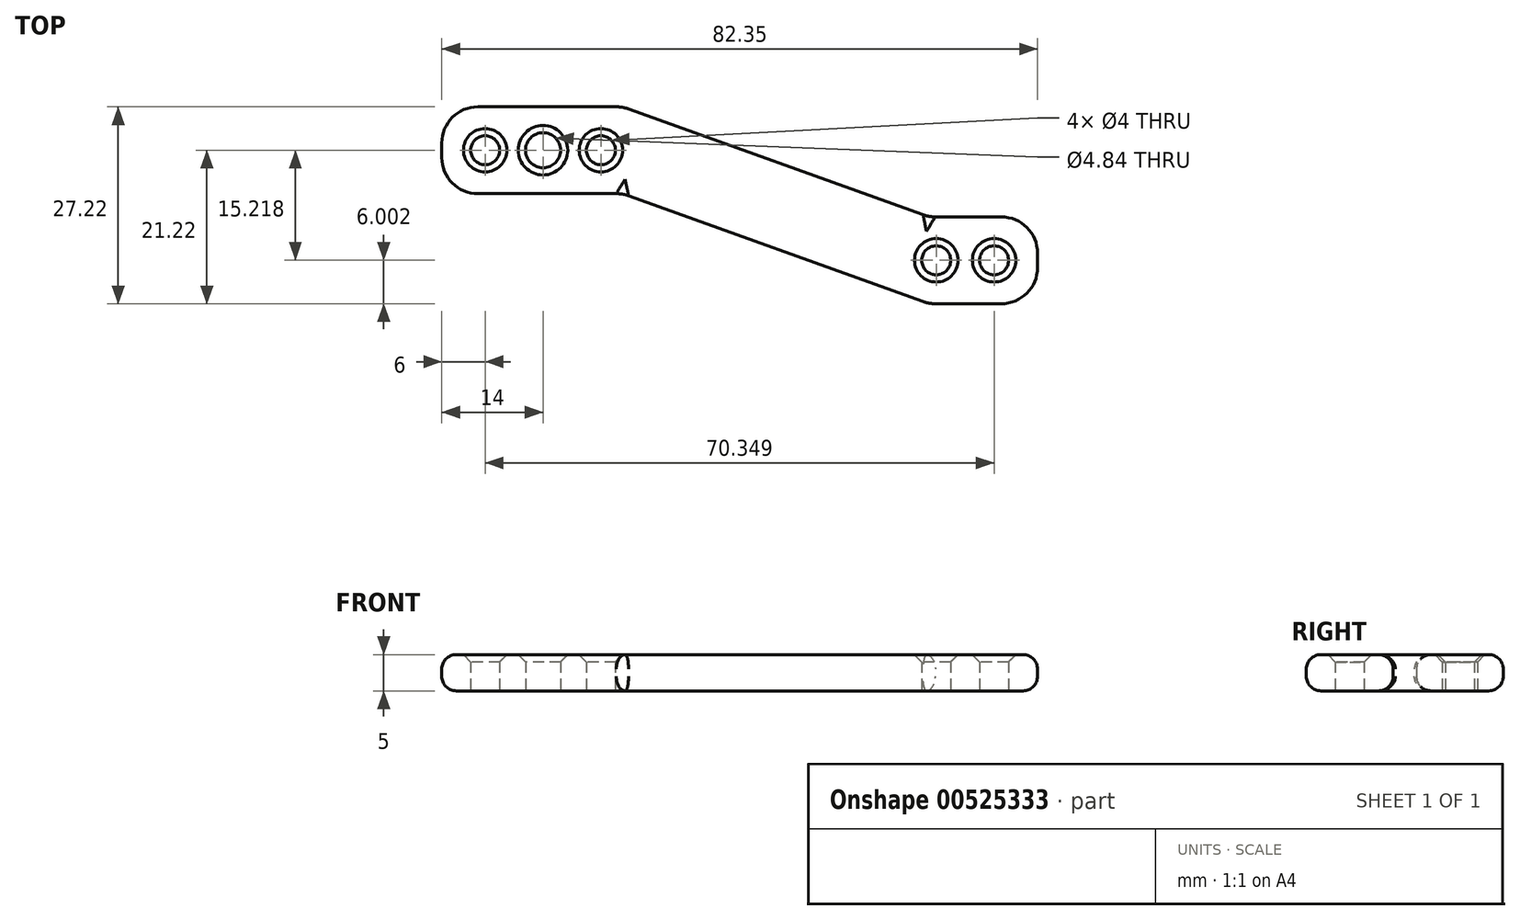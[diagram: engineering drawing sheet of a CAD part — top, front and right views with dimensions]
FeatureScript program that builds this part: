
annotation { "Feature Type Name" : "Feature", "Feature Type Description" : "" }
export const myFeature = defineFeature(function(context is Context, id is Id, definition is map)
    precondition{}
    {
        {
            var Q0;
            Q0=qCreatedBy(makeId("Top.planeOp"),FACE);
            var sketch = newSketch(context, id + "F0", { "sketchPlane" : qUnion([Q0])});
            skLineSegment(sketch, "E0.bottom", {"start": v(0, 0) * mm, "end": v(25, 0) * mm});
            skLineSegment(sketch, "E0.top", {"start": v(0, -12) * mm, "end": v(25, -12) * mm});
            skLineSegment(sketch, "E0.left", {"start": v(0, 0) * mm, "end": v(0, -12) * mm});
            skLineSegment(sketch, "E0.right", {"start": v(25, 0) * mm, "end": v(25, -12) * mm});
            skLineSegment(sketch, "E1", {"start": v(25, -12) * mm, "end": v(67.35, -27.22) * mm});
            skLineSegment(sketch, "E2", {"start": v(25, 0) * mm, "end": v(67.35, -15.22) * mm});
            skLineSegment(sketch, "E3", {"start": v(67.35, -15.22) * mm, "end": v(67.35, -27.22) * mm});
            skLineSegment(sketch, "E4.bottom", {"start": v(67.35, -27.22) * mm, "end": v(82.35, -27.22) * mm});
            skLineSegment(sketch, "E4.top", {"start": v(67.35, -15.22) * mm, "end": v(82.35, -15.22) * mm});
            skLineSegment(sketch, "E4.left", {"start": v(67.35, -27.22) * mm, "end": v(67.35, -15.22) * mm});
            skLineSegment(sketch, "E4.right", {"start": v(82.35, -27.22) * mm, "end": v(82.35, -15.22) * mm});
            skSolve(sketch);
        }
        {
            var Q0;
            Q0 = qSketchRegion(id + "F0", true);
            extrude(context, id + "F1", {"entities" : qUnion([Q0]), "depth" : 5 * mm, "offsetDistance" : 25 * mm});
        }
        {
            var Q0;
            Q0=qCreatedBy(makeId("Top.planeOp"),FACE);
            var sketch = newSketch(context, id + "F2", { "sketchPlane" : qUnion([Q0])});
            skCircle(sketch, "E5", {"center": v(6, -6) * mm, "radius": 2 * mm});
            skCircle(sketch, "E6", {"center": v(76.35, -21.22) * mm, "radius": 2 * mm});
            skCircle(sketch, "E7", {"center": v(14, -6) * mm, "radius": 2.42 * mm});
            skCircle(sketch, "E8", {"center": v(22, -6) * mm, "radius": 2 * mm});
            skCircle(sketch, "E9", {"center": v(68.35, -21.22) * mm, "radius": 2 * mm});
            skSolve(sketch);
        }
        {
            var Q0;
            Q0 = qSketchRegion(id + "F2", true);
            extrude(context, id + "F3", {"entities" : qUnion([Q0]), "operationType" : NewBodyOperationType.REMOVE, "depth" : 50 * mm, "offsetDistance" : 25 * mm});
        }
        {
            var Q0;
            Q0=makeQuery(id+"F1.opExtrude","CAP_EDGE",EDGE,{"disambiguationData":[OSD([sQuery(id+"F0.wireOp",EDGE,"E2")])],"isStart":false});
            var Q1;
            Q1=makeQuery(id+"F1.opExtrude","CAP_EDGE",EDGE,{"disambiguationData":[OSD([sQuery(id+"F0.wireOp",EDGE,"E0.bottom")])],"isStart":false});
            var Q2;
            Q2=makeQuery(id+"F1.opExtrude","CAP_EDGE",EDGE,{"disambiguationData":[OSD([sQuery(id+"F0.wireOp",EDGE,"E0.left")])],"isStart":false});
            var Q3;
            Q3=makeQuery(id+"F1.opExtrude","CAP_EDGE",EDGE,{"disambiguationData":[OSD([sQuery(id+"F0.wireOp",EDGE,"E0.top")])],"isStart":false});
            var Q4;
            Q4=makeQuery(id+"F1.opExtrude","CAP_EDGE",EDGE,{"disambiguationData":[OSD([sQuery(id+"F0.wireOp",EDGE,"E1")])],"isStart":false});
            var Q5;
            Q5=makeQuery(id+"F1.opExtrude","CAP_EDGE",EDGE,{"disambiguationData":[OSD([sQuery(id+"F0.wireOp",EDGE,"E4.bottom")])],"isStart":false});
            var Q6;
            Q6=makeQuery(id+"F1.opExtrude","CAP_EDGE",EDGE,{"disambiguationData":[OSD([sQuery(id+"F0.wireOp",EDGE,"E4.right")])],"isStart":false});
            var Q7;
            Q7=makeQuery(id+"F1.opExtrude","CAP_EDGE",EDGE,{"disambiguationData":[OSD([sQuery(id+"F0.wireOp",EDGE,"E4.top")])],"isStart":false});
            var Q8;
            Q8=makeQuery(id+"F1.opExtrude","CAP_EDGE",EDGE,{"disambiguationData":[OSD([sQuery(id+"F0.wireOp",EDGE,"E1")])],"isStart":true});
            var Q9;
            Q9=makeQuery(id+"F1.opExtrude","CAP_EDGE",EDGE,{"disambiguationData":[OSD([sQuery(id+"F0.wireOp",EDGE,"E0.top")])],"isStart":true});
            var Q10;
            Q10=makeQuery(id+"F1.opExtrude","CAP_EDGE",EDGE,{"disambiguationData":[OSD([sQuery(id+"F0.wireOp",EDGE,"E0.left")])],"isStart":true});
            var Q11;
            Q11=makeQuery(id+"F1.opExtrude","CAP_EDGE",EDGE,{"disambiguationData":[OSD([sQuery(id+"F0.wireOp",EDGE,"E0.bottom")])],"isStart":true});
            var Q12;
            Q12=makeQuery(id+"F1.opExtrude","CAP_EDGE",EDGE,{"disambiguationData":[OSD([sQuery(id+"F0.wireOp",EDGE,"E2")])],"isStart":true});
            var Q13;
            Q13=makeQuery(id+"F1.opExtrude","CAP_EDGE",EDGE,{"disambiguationData":[OSD([sQuery(id+"F0.wireOp",EDGE,"E4.top")])],"isStart":true});
            var Q14;
            Q14=makeQuery(id+"F1.opExtrude","CAP_EDGE",EDGE,{"disambiguationData":[OSD([sQuery(id+"F0.wireOp",EDGE,"E4.right")])],"isStart":true});
            var Q15;
            Q15=makeQuery(id+"F1.opExtrude","CAP_EDGE",EDGE,{"disambiguationData":[OSD([sQuery(id+"F0.wireOp",EDGE,"E4.bottom")])],"isStart":true});
            fillet(context, id + "F4", {"entities" : qUnion([Q0, Q1, Q2, Q3, Q4, Q5, Q6, Q7, Q8, Q9, Q10, Q11, Q12, Q13, Q14, Q15]), "radius" : 2 * mm, "tangentPropagation" : true, "allowEdgeOverflow" : false});
        }
        {
            var Q0;
            Q0=makeQuery(id+"F4.opFillet","BLEND_EDGE",EDGE,{"blendedFrom":[makeQuery(id+"F1.opExtrude","CAP_EDGE",EDGE,{"disambiguationData":[OSD([sQuery(id+"F0.wireOp",EDGE,"E0.top")])],"isStart":true}),makeQuery(id+"F1.opExtrude","CAP_EDGE",EDGE,{"disambiguationData":[OSD([sQuery(id+"F0.wireOp",EDGE,"E1")])],"isStart":true})],"blendedInto":[]});
            var Q1;
            Q1=makeQuery(id+"F1.opExtrude","SWEPT_EDGE",EDGE,{"disambiguationData":[OSD([sQuery(id+"F0.wireOp",EDGE,"E0.top"),sQuery(id+"F0.wireOp",EDGE,"E0.right"),sQuery(id+"F0.wireOp",EDGE,"E1")])]});
            var Q2;
            Q2=makeQuery(id+"F4.opFillet","BLEND_EDGE",EDGE,{"blendedFrom":[makeQuery(id+"F1.opExtrude","CAP_EDGE",EDGE,{"disambiguationData":[OSD([sQuery(id+"F0.wireOp",EDGE,"E0.top")])],"isStart":false}),makeQuery(id+"F1.opExtrude","CAP_EDGE",EDGE,{"disambiguationData":[OSD([sQuery(id+"F0.wireOp",EDGE,"E1")])],"isStart":false})],"blendedInto":[]});
            var Q3;
            Q3=makeQuery(id+"F4.opFillet","BLEND_EDGE",EDGE,{"blendedFrom":[makeQuery(id+"F1.opExtrude","CAP_EDGE",EDGE,{"disambiguationData":[OSD([sQuery(id+"F0.wireOp",EDGE,"E0.bottom")])],"isStart":true}),makeQuery(id+"F1.opExtrude","CAP_EDGE",EDGE,{"disambiguationData":[OSD([sQuery(id+"F0.wireOp",EDGE,"E2")])],"isStart":true})],"blendedInto":[]});
            var Q4;
            Q4=makeQuery(id+"F4.opFillet","BLEND_EDGE",EDGE,{"blendedFrom":[makeQuery(id+"F1.opExtrude","CAP_EDGE",EDGE,{"disambiguationData":[OSD([sQuery(id+"F0.wireOp",EDGE,"E1")])],"isStart":false}),makeQuery(id+"F1.opExtrude","CAP_EDGE",EDGE,{"disambiguationData":[OSD([sQuery(id+"F0.wireOp",EDGE,"E4.bottom")])],"isStart":false})],"blendedInto":[]});
            var Q5;
            Q5=makeQuery(id+"F4.opFillet","BLEND_EDGE",EDGE,{"blendedFrom":[makeQuery(id+"F1.opExtrude","CAP_EDGE",EDGE,{"disambiguationData":[OSD([sQuery(id+"F0.wireOp",EDGE,"E2")])],"isStart":true}),makeQuery(id+"F1.opExtrude","CAP_EDGE",EDGE,{"disambiguationData":[OSD([sQuery(id+"F0.wireOp",EDGE,"E4.top")])],"isStart":true})],"blendedInto":[]});
            var Q6;
            Q6=makeQuery(id+"F4.opFillet","BLEND_EDGE",EDGE,{"blendedFrom":[makeQuery(id+"F1.opExtrude","CAP_EDGE",EDGE,{"disambiguationData":[OSD([sQuery(id+"F0.wireOp",EDGE,"E2")])],"isStart":false}),makeQuery(id+"F1.opExtrude","CAP_EDGE",EDGE,{"disambiguationData":[OSD([sQuery(id+"F0.wireOp",EDGE,"E4.top")])],"isStart":false})],"blendedInto":[]});
            var Q7;
            Q7=makeQuery(id+"F4.opFillet","BLEND_EDGE",EDGE,{"blendedFrom":[makeQuery(id+"F1.opExtrude","CAP_EDGE",EDGE,{"disambiguationData":[OSD([sQuery(id+"F0.wireOp",EDGE,"E0.bottom")])],"isStart":false}),makeQuery(id+"F1.opExtrude","CAP_EDGE",EDGE,{"disambiguationData":[OSD([sQuery(id+"F0.wireOp",EDGE,"E2")])],"isStart":false})],"blendedInto":[]});
            var Q8;
            Q8=makeQuery(id+"F4.opFillet","BLEND_EDGE",EDGE,{"blendedFrom":[makeQuery(id+"F1.opExtrude","CAP_EDGE",EDGE,{"disambiguationData":[OSD([sQuery(id+"F0.wireOp",EDGE,"E1")])],"isStart":true}),makeQuery(id+"F1.opExtrude","CAP_EDGE",EDGE,{"disambiguationData":[OSD([sQuery(id+"F0.wireOp",EDGE,"E4.bottom")])],"isStart":true})],"blendedInto":[]});
            fillet(context, id + "F5", {"entities" : qUnion([Q0, Q1, Q2, Q3, Q4, Q5, Q6, Q7, Q8]), "radius" : 5 * mm, "tangentPropagation" : true, "allowEdgeOverflow" : false});
        }
        {
            var Q0;
            Q0=makeQuery(id+"F4.opFillet","BLEND_EDGE",EDGE,{"blendedFrom":[makeQuery(id+"F1.opExtrude","CAP_EDGE",EDGE,{"disambiguationData":[OSD([sQuery(id+"F0.wireOp",EDGE,"E4.bottom")])],"isStart":false}),makeQuery(id+"F1.opExtrude","CAP_EDGE",EDGE,{"disambiguationData":[OSD([sQuery(id+"F0.wireOp",EDGE,"E4.right")])],"isStart":false})],"blendedInto":[]});
            var Q1;
            Q1=makeQuery(id+"F4.opFillet","BLEND_EDGE",EDGE,{"blendedFrom":[makeQuery(id+"F1.opExtrude","CAP_EDGE",EDGE,{"disambiguationData":[OSD([sQuery(id+"F0.wireOp",EDGE,"E0.top")])],"isStart":false}),makeQuery(id+"F1.opExtrude","CAP_EDGE",EDGE,{"disambiguationData":[OSD([sQuery(id+"F0.wireOp",EDGE,"E0.left")])],"isStart":false})],"blendedInto":[]});
            var Q2;
            Q2=makeQuery(id+"F4.opFillet","BLEND_EDGE",EDGE,{"blendedFrom":[makeQuery(id+"F1.opExtrude","CAP_EDGE",EDGE,{"disambiguationData":[OSD([sQuery(id+"F0.wireOp",EDGE,"E0.bottom")])],"isStart":true}),makeQuery(id+"F1.opExtrude","CAP_EDGE",EDGE,{"disambiguationData":[OSD([sQuery(id+"F0.wireOp",EDGE,"E0.left")])],"isStart":true})],"blendedInto":[]});
            var Q3;
            Q3=makeQuery(id+"F4.opFillet","BLEND_EDGE",EDGE,{"blendedFrom":[makeQuery(id+"F1.opExtrude","CAP_EDGE",EDGE,{"disambiguationData":[OSD([sQuery(id+"F0.wireOp",EDGE,"E4.top")])],"isStart":false}),makeQuery(id+"F1.opExtrude","CAP_EDGE",EDGE,{"disambiguationData":[OSD([sQuery(id+"F0.wireOp",EDGE,"E4.right")])],"isStart":false})],"blendedInto":[]});
            var Q4;
            Q4=makeQuery(id+"F4.opFillet","BLEND_EDGE",EDGE,{"blendedFrom":[makeQuery(id+"F1.opExtrude","CAP_EDGE",EDGE,{"disambiguationData":[OSD([sQuery(id+"F0.wireOp",EDGE,"E4.bottom")])],"isStart":true}),makeQuery(id+"F1.opExtrude","CAP_EDGE",EDGE,{"disambiguationData":[OSD([sQuery(id+"F0.wireOp",EDGE,"E4.right")])],"isStart":true})],"blendedInto":[]});
            var Q5;
            Q5=makeQuery(id+"F4.opFillet","BLEND_EDGE",EDGE,{"blendedFrom":[makeQuery(id+"F1.opExtrude","CAP_EDGE",EDGE,{"disambiguationData":[OSD([sQuery(id+"F0.wireOp",EDGE,"E4.top")])],"isStart":true}),makeQuery(id+"F1.opExtrude","CAP_EDGE",EDGE,{"disambiguationData":[OSD([sQuery(id+"F0.wireOp",EDGE,"E4.right")])],"isStart":true})],"blendedInto":[]});
            fillet(context, id + "F6", {"entities" : qUnion([Q0, Q1, Q2, Q3, Q4, Q5]), "radius" : 5 * mm, "tangentPropagation" : true, "allowEdgeOverflow" : false});
        }
        {
            var Q0;
            Q0=makeQuery(id+"F3.boolean.opBoolean","INTERSECT",EDGE,{"derivedFrom":[makeQuery(id+"F1.opExtrude","CAP_FACE",FACE,{"disambiguationData":[OSD([sQuery(id+"F0.wireOp",EDGE,"E0.bottom"),sQuery(id+"F0.wireOp",EDGE,"E0.top"),sQuery(id+"F0.wireOp",EDGE,"E0.left"),sQuery(id+"F0.wireOp",EDGE,"E1"),sQuery(id+"F0.wireOp",EDGE,"E2"),sQuery(id+"F0.wireOp",EDGE,"E4.bottom"),sQuery(id+"F0.wireOp",EDGE,"E4.top"),sQuery(id+"F0.wireOp",EDGE,"E4.right")])],"isStart":false}),makeQuery(id+"F3.opExtrude","SWEPT_FACE",FACE,{"disambiguationData":[OSD([sQuery(id+"F2.wireOp",EDGE,"E5")])]})]});
            var Q1;
            Q1=makeQuery(id+"F3.boolean.opBoolean","INTERSECT",EDGE,{"derivedFrom":[makeQuery(id+"F1.opExtrude","CAP_FACE",FACE,{"disambiguationData":[OSD([sQuery(id+"F0.wireOp",EDGE,"E0.bottom"),sQuery(id+"F0.wireOp",EDGE,"E0.top"),sQuery(id+"F0.wireOp",EDGE,"E0.left"),sQuery(id+"F0.wireOp",EDGE,"E1"),sQuery(id+"F0.wireOp",EDGE,"E2"),sQuery(id+"F0.wireOp",EDGE,"E4.bottom"),sQuery(id+"F0.wireOp",EDGE,"E4.top"),sQuery(id+"F0.wireOp",EDGE,"E4.right")])],"isStart":false}),makeQuery(id+"F3.opExtrude","SWEPT_FACE",FACE,{"disambiguationData":[OSD([sQuery(id+"F2.wireOp",EDGE,"E7")])]})]});
            var Q2;
            Q2=makeQuery(id+"F3.boolean.opBoolean","INTERSECT",EDGE,{"derivedFrom":[makeQuery(id+"F1.opExtrude","CAP_FACE",FACE,{"disambiguationData":[OSD([sQuery(id+"F0.wireOp",EDGE,"E0.bottom"),sQuery(id+"F0.wireOp",EDGE,"E0.top"),sQuery(id+"F0.wireOp",EDGE,"E0.left"),sQuery(id+"F0.wireOp",EDGE,"E1"),sQuery(id+"F0.wireOp",EDGE,"E2"),sQuery(id+"F0.wireOp",EDGE,"E4.bottom"),sQuery(id+"F0.wireOp",EDGE,"E4.top"),sQuery(id+"F0.wireOp",EDGE,"E4.right")])],"isStart":false}),makeQuery(id+"F3.opExtrude","SWEPT_FACE",FACE,{"disambiguationData":[OSD([sQuery(id+"F2.wireOp",EDGE,"E8")])]})]});
            var Q3;
            Q3=makeQuery(id+"F3.boolean.opBoolean","INTERSECT",EDGE,{"derivedFrom":[makeQuery(id+"F1.opExtrude","CAP_FACE",FACE,{"disambiguationData":[OSD([sQuery(id+"F0.wireOp",EDGE,"E0.bottom"),sQuery(id+"F0.wireOp",EDGE,"E0.top"),sQuery(id+"F0.wireOp",EDGE,"E0.left"),sQuery(id+"F0.wireOp",EDGE,"E1"),sQuery(id+"F0.wireOp",EDGE,"E2"),sQuery(id+"F0.wireOp",EDGE,"E4.bottom"),sQuery(id+"F0.wireOp",EDGE,"E4.top"),sQuery(id+"F0.wireOp",EDGE,"E4.right")])],"isStart":false}),makeQuery(id+"F3.opExtrude","SWEPT_FACE",FACE,{"disambiguationData":[OSD([sQuery(id+"F2.wireOp",EDGE,"E9")])]})]});
            var Q4;
            Q4=makeQuery(id+"F3.boolean.opBoolean","INTERSECT",EDGE,{"derivedFrom":[makeQuery(id+"F1.opExtrude","CAP_FACE",FACE,{"disambiguationData":[OSD([sQuery(id+"F0.wireOp",EDGE,"E0.bottom"),sQuery(id+"F0.wireOp",EDGE,"E0.top"),sQuery(id+"F0.wireOp",EDGE,"E0.left"),sQuery(id+"F0.wireOp",EDGE,"E1"),sQuery(id+"F0.wireOp",EDGE,"E2"),sQuery(id+"F0.wireOp",EDGE,"E4.bottom"),sQuery(id+"F0.wireOp",EDGE,"E4.top"),sQuery(id+"F0.wireOp",EDGE,"E4.right")])],"isStart":false}),makeQuery(id+"F3.opExtrude","SWEPT_FACE",FACE,{"disambiguationData":[OSD([sQuery(id+"F2.wireOp",EDGE,"E6")])]})]});
            chamfer(context, id + "F7", {"entities" : qUnion([Q0, Q1, Q2, Q3, Q4]), "width" : 1 * mm, "tangentPropagation" : true});
        }
    });
